# Revit family: ok-Celite_City_Bacia Convencional_20301
name_source: partatom
category: Plumbing Fixtures
revit_build: Autodesk Revit MEP 2014 (Build: 20131024_2115(x64)
units: mm (PartAtom-declared; Revit-internal decimal feet)

## types (4) — shared parameters
Assembly Code = D2010100
Bolsa para bacia = Bolsa tubo para bacia convencional (00638), Acessórios - Metais Celite
CWFU = 1
Celite: Categoria = Linhas Completas
Celite: Código = 20301
Celite: Fabricante = Celite
Celite: Linha = City
Celite: Link do Produto = http://www.celite.com.br
Celite: Norma = ABNT NBR 15097-1: 2011 / ABNT NBR 15097-2: 2011 - fabricação/instalação
Celite: Produto = Louças
Celite: Tipo = Bacias convencionais
Celite: Versão = Autodesk Revit MEP 2014
Desenvolvido por = ofcdesk
Diâmetro Ponto de Esgoto = 100 mm
Manufacturer = Celite
Model = 20301
Raio Ponto de Esgoto = 50 mm
Raio Ponto de Água = 20 mm
Selo de Qualidade ofcdesk = Standard
URL = http://www.celite.com.br
WFU = 3
zero-valued in all types: Default Elevation

## per-type parameters (varying)
| type | Celite: Cores Disponíveis | Celite: Descrição | Description | Tipo do assento |
| Branca - 20301 com Assento Universal PP | Branco | Bacia convencional cor branca (20301), linha City - Louças Celite | Bacia convencional cor branca (20301), linha City - Louças Celite | Celite_City_Assento para Bacia Sanitária_20981 : Branco - 20981 |
| Preta - 20301 com Assento Universal PP | Preto | Bacia convencional cor preta (20301), linha City - Louças Celite | Bacia convencional cor preta (20301), linha City - Louças Celite | Celite_City_Assento para Bacia Sanitária_20981 : Preto - 20981 |
| Pergamon - 20301 com Assento Universal PP | Pergamon | Bacia convencional cor pergamon (20301), linha City - Louças Celite | Bacia convencional cor pergamon (20301), linha City - Louças Celite | Celite_City_Assento para Bacia Sanitária_20981 : Pergamon - 20981 |
| Cinza prata - 20301 com Assento Universal PP | Cinza prata | Bacia convencional cor cinza prata (20301), linha City - Louças Celite | Bacia convencional cor cinza prata (20301), linha City - Louças Celite | Celite_City_Assento para Bacia Sanitária_20981 : Cinza prata - 20981 |

## geometry (parser evidence)
native form markers: Blend x2, Sweep x8
no freeform markers — native parametric forms only
